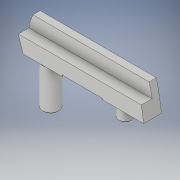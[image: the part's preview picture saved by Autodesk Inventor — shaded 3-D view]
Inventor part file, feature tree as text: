
AUTODESK INVENTOR PART (.ipt)
format: ipt  version: 2018.3 (Build 223284000, 284)  size: 189,440 bytes
history: native  units: in
note: dims shown in document units (in); Inventor stores cm internally (conversion verified against a paired STEP export)
features: sketch x5, revolve x3, extrude x2, plane x2
ambient origin geometry x8: Origin, YZ Plane, XZ Plane, XY Plane, X Axis, Y Axis, Z Axis, Center Point
bodies: Solid1 (feature_tree)
feature tree (12):
  sketch  "Sketch1"  dims[d0=0.02in d1=0.481in]
  extrude  "Extrusion1"  Depth=0.02in
  revolve  "Revolution1"  [1 undecoded]
  plane  "Work Plane1"
  extrude  "Extrusion2"  Depth=0.964in
  plane  "Work Plane2"
  revolve  "Revolution2"  [1 undecoded]
  revolve  "Revolution3"  [1 undecoded]
  sketch  "Sketch2"  dims[d3=3.626in d4=0.135in]
  sketch  "Sketch3"  dims[d5=0.22in d6=0.964in]
  sketch  "Sketch4"  dims[d7=0.312in d8=0.18in]
  sketch  "Sketch5"  dims[d9=0.784in d10=0.585in d11=0.01in d12=0.156in d13=0.1202in d14=0.138in d15=0.0in d16=0.0623in d17=0.32in d18=0.01in d19=45.0deg d20=90.0deg d21=0.012in d22=0.18in d23=-0.02in d24=0.138in d25=0.056in d26=0.138in d27=0.0in d28=0.013in d29=0.012in d30=0.765in d31=0.0483in d32=0.09in d33=0.01in d34=45.0deg d35=90.0deg d36=3.626in d37=90.0deg]
note: 3 required parameter values undecoded (feature->parameter linkage not recoverable at this tier; creation-order binding heuristic only, values carry confidence <= 0.55)
